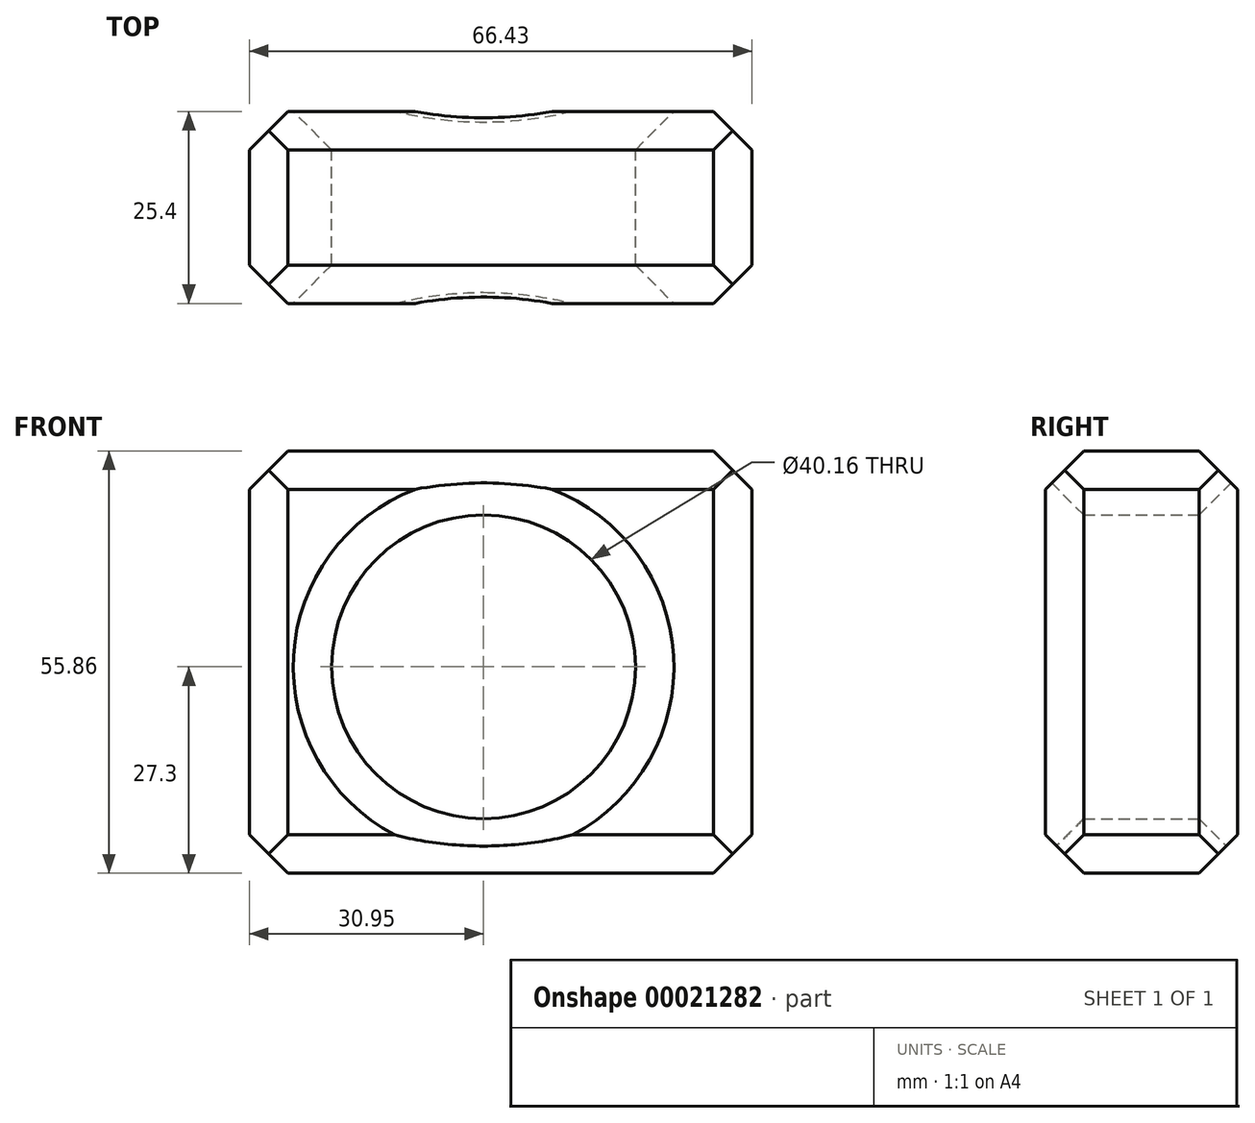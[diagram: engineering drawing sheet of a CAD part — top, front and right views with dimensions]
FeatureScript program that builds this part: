
annotation { "Feature Type Name" : "Feature", "Feature Type Description" : "" }
export const myFeature = defineFeature(function(context is Context, id is Id, definition is map)
    precondition{}
    {
        {
            var Q0;
            Q0=qCreatedBy(makeId("Front.planeOp"),FACE);
            var sketch = newSketch(context, id + "F0", { "sketchPlane" : qUnion([Q0])});
            skLineSegment(sketch, "E0.bottom", {"start": v(-30.95, 28.56) * mm, "end": v(35.48, 28.56) * mm});
            skLineSegment(sketch, "E0.top", {"start": v(-30.95, -27.3) * mm, "end": v(35.48, -27.3) * mm});
            skLineSegment(sketch, "E0.left", {"start": v(-30.95, 28.56) * mm, "end": v(-30.95, -27.3) * mm});
            skLineSegment(sketch, "E0.right", {"start": v(35.48, 28.56) * mm, "end": v(35.48, -27.3) * mm});
            skCircle(sketch, "E1", {"center": v(0, 0) * mm, "radius": 20.08 * mm});
            skSolve(sketch);
        }
        {
            var Q0;
            Q0=makeQuery(id+"F0.imprint","IMPRINT",FACE,{"disambiguationData":[TD([[makeQuery(id+"F0.imprint","IMPRINT",EDGE,{"derivedFrom":sQuery(id+"F0.wireOp",EDGE,"E0.bottom")}),-1.0]])]});
            extrude(context, id + "F1", {"entities" : qUnion([Q0]), "depth" : 25.4 * mm});
        }
        {
            var Q0;
            Q0=makeQuery(id+"F1.opExtrude","CAP_EDGE",EDGE,{"disambiguationData":[OSD([sQuery(id+"F0.wireOp",EDGE,"E1")])],"isStart":false});
            var Q1;
            Q1=makeQuery(id+"F1.opExtrude","CAP_EDGE",EDGE,{"disambiguationData":[OSD([sQuery(id+"F0.wireOp",EDGE,"E1")])],"isStart":true});
            chamfer(context, id + "F2", {"entities" : qUnion([Q0, Q1]), "width" : 5.08 * mm, "tangentPropagation" : true});
        }
        {
            var Q0;
            Q0=makeQuery(id+"F1.opExtrude","CAP_EDGE",EDGE,{"disambiguationData":[OSD([sQuery(id+"F0.wireOp",EDGE,"E0.right")])],"isStart":false});
            chamfer(context, id + "F3", {"entities" : qUnion([Q0]), "width" : 5.08 * mm, "tangentPropagation" : true});
        }
        {
            var Q0;
            Q0=makeQuery(id+"F1.opExtrude","CAP_EDGE",EDGE,{"disambiguationData":[OSD([sQuery(id+"F0.wireOp",EDGE,"E0.right")])],"isStart":true});
            chamfer(context, id + "F4", {"entities" : qUnion([Q0]), "width" : 5.08 * mm, "tangentPropagation" : true});
        }
        {
            var Q0;
            Q0=makeQuery(id+"F1.opExtrude","SWEPT_EDGE",EDGE,{"disambiguationData":[OSD([sQuery(id+"F0.wireOp",EDGE,"E0.bottom"),sQuery(id+"F0.wireOp",EDGE,"E0.right")])]});
            chamfer(context, id + "F5", {"entities" : qUnion([Q0]), "width" : 5.08 * mm, "tangentPropagation" : true});
        }
        {
            var Q0;
            Q0=makeQuery(id+"F1.opExtrude","CAP_EDGE",EDGE,{"disambiguationData":[OSD([sQuery(id+"F0.wireOp",EDGE,"E0.top")])],"isStart":false});
            chamfer(context, id + "F6", {"entities" : qUnion([Q0]), "width" : 5.08 * mm, "tangentPropagation" : true});
        }
        {
            var Q0;
            Q0=makeQuery(id+"F1.opExtrude","CAP_EDGE",EDGE,{"disambiguationData":[OSD([sQuery(id+"F0.wireOp",EDGE,"E0.top")])],"isStart":true});
            chamfer(context, id + "F7", {"entities" : qUnion([Q0]), "width" : 5.08 * mm, "tangentPropagation" : true});
        }
        {
            var Q0;
            Q0=makeQuery(id+"F1.opExtrude","SWEPT_EDGE",EDGE,{"disambiguationData":[OSD([sQuery(id+"F0.wireOp",EDGE,"E0.top"),sQuery(id+"F0.wireOp",EDGE,"E0.right")])]});
            chamfer(context, id + "F8", {"entities" : qUnion([Q0]), "width" : 5.08 * mm, "tangentPropagation" : true});
        }
        {
            var Q0;
            Q0=makeQuery(id+"F1.opExtrude","CAP_EDGE",EDGE,{"disambiguationData":[OSD([sQuery(id+"F0.wireOp",EDGE,"E0.left")])],"isStart":false});
            chamfer(context, id + "F9", {"entities" : qUnion([Q0]), "width" : 5.08 * mm, "tangentPropagation" : true});
        }
        {
            var Q0;
            Q0=makeQuery(id+"F1.opExtrude","SWEPT_EDGE",EDGE,{"disambiguationData":[OSD([sQuery(id+"F0.wireOp",EDGE,"E0.top"),sQuery(id+"F0.wireOp",EDGE,"E0.left")])]});
            chamfer(context, id + "F10", {"entities" : qUnion([Q0]), "width" : 5.08 * mm, "tangentPropagation" : true});
        }
        {
            var Q0;
            Q0=makeQuery(id+"F1.opExtrude","CAP_EDGE",EDGE,{"disambiguationData":[OSD([sQuery(id+"F0.wireOp",EDGE,"E0.left")])],"isStart":true});
            chamfer(context, id + "F11", {"entities" : qUnion([Q0]), "width" : 5.08 * mm, "tangentPropagation" : true});
        }
        {
            var Q0;
            Q0=makeQuery(id+"F1.opExtrude","CAP_EDGE",EDGE,{"disambiguationData":[OSD([sQuery(id+"F0.wireOp",EDGE,"E0.bottom")])],"isStart":false});
            chamfer(context, id + "F12", {"entities" : qUnion([Q0]), "width" : 5.08 * mm, "tangentPropagation" : true});
        }
        {
            var Q0;
            Q0=makeQuery(id+"F1.opExtrude","SWEPT_EDGE",EDGE,{"disambiguationData":[OSD([sQuery(id+"F0.wireOp",EDGE,"E0.bottom"),sQuery(id+"F0.wireOp",EDGE,"E0.left")])]});
            chamfer(context, id + "F13", {"entities" : qUnion([Q0]), "width" : 5.08 * mm, "tangentPropagation" : true});
        }
        {
            var Q0;
            Q0=makeQuery(id+"F1.opExtrude","CAP_EDGE",EDGE,{"disambiguationData":[OSD([sQuery(id+"F0.wireOp",EDGE,"E0.bottom")])],"isStart":true});
            chamfer(context, id + "F14", {"entities" : qUnion([Q0]), "width" : 5.08 * mm, "tangentPropagation" : true});
        }
    });
